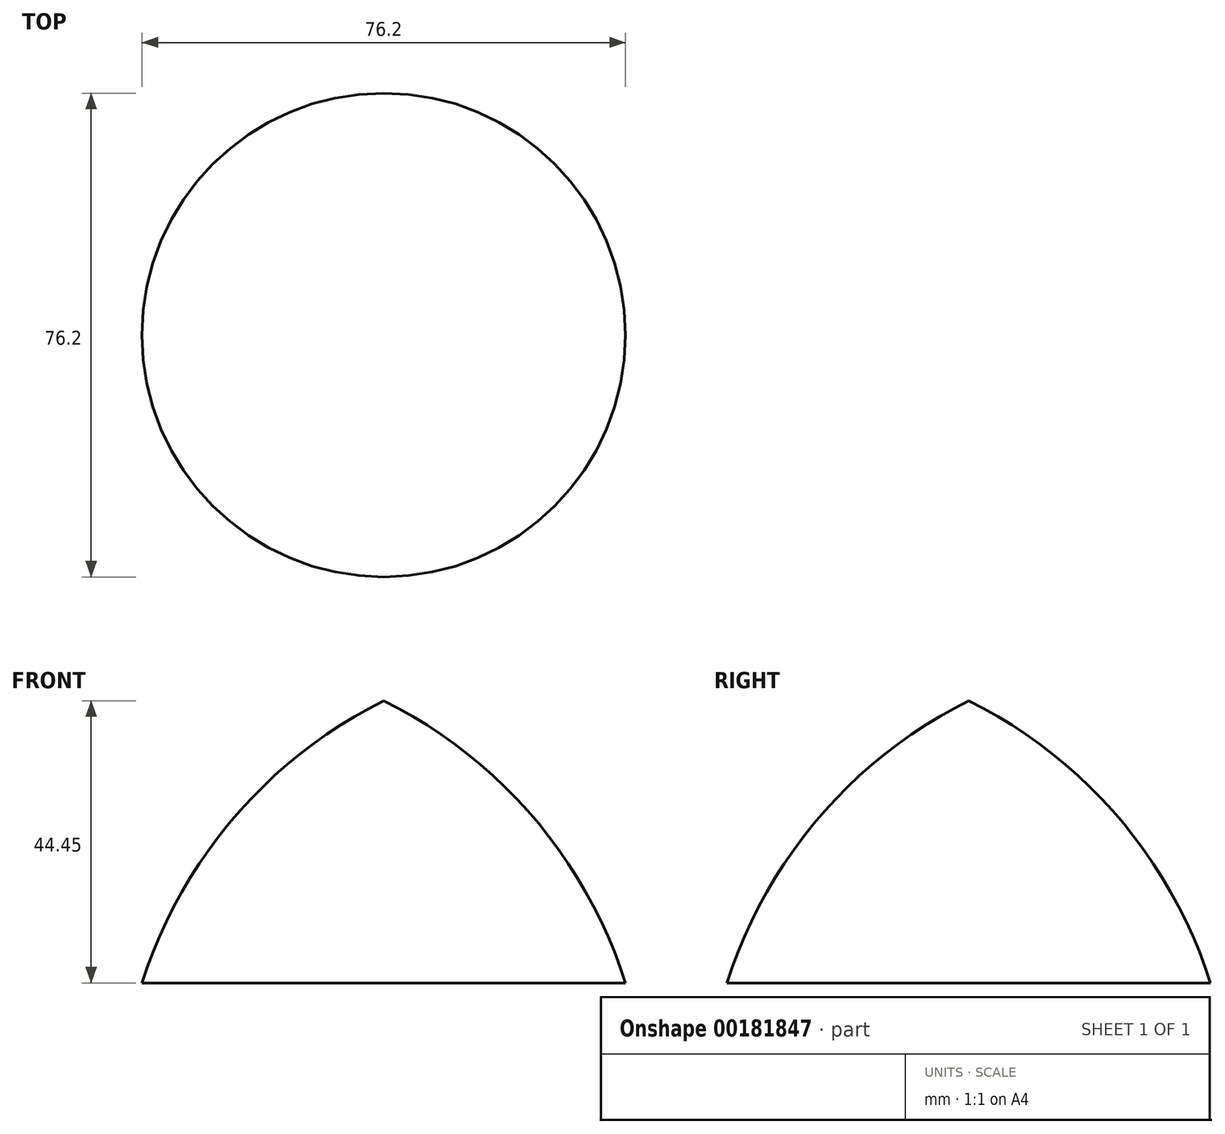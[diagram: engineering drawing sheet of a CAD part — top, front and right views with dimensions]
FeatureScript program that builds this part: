
annotation { "Feature Type Name" : "Feature", "Feature Type Description" : "" }
export const myFeature = defineFeature(function(context is Context, id is Id, definition is map)
    precondition{}
    {
        {
            var Q0;
            Q0=qCreatedBy(makeId("Right.planeOp"),FACE);
            var sketch = newSketch(context, id + "F0", { "sketchPlane" : qUnion([Q0])});
            skLineSegment(sketch, "E0", {"start": v(0, 55.76) * mm, "end": v(0, 11.31) * mm});
            skLineSegment(sketch, "E1", {"start": v(0, 11.31) * mm, "end": v(38.1, 11.31) * mm});
            skArc(sketch, "E2", {"start": v(38.1, 11.31) * mm, "mid": v(23.56, 37.4) * mm, "end": v(0, 55.76) * mm});
            skSolve(sketch);
        }
        {
            var Q0;
            Q0=makeQuery(id+"F0.imprint","IMPRINT",FACE,{"disambiguationData":[TD([[makeQuery(id+"F0.imprint","IMPRINT",EDGE,{"derivedFrom":sQuery(id+"F0.wireOp",EDGE,"E0")}),1.0]])]});
            var Q1;
            Q1=sQuery(id+"F0.wireOp",EDGE,"E0");
            revolve(context, id + "F1", {"entities" : qUnion([Q0]), "axis" : qUnion([Q1]), "revolveType" : RevolveType.FULL});
        }
    });
